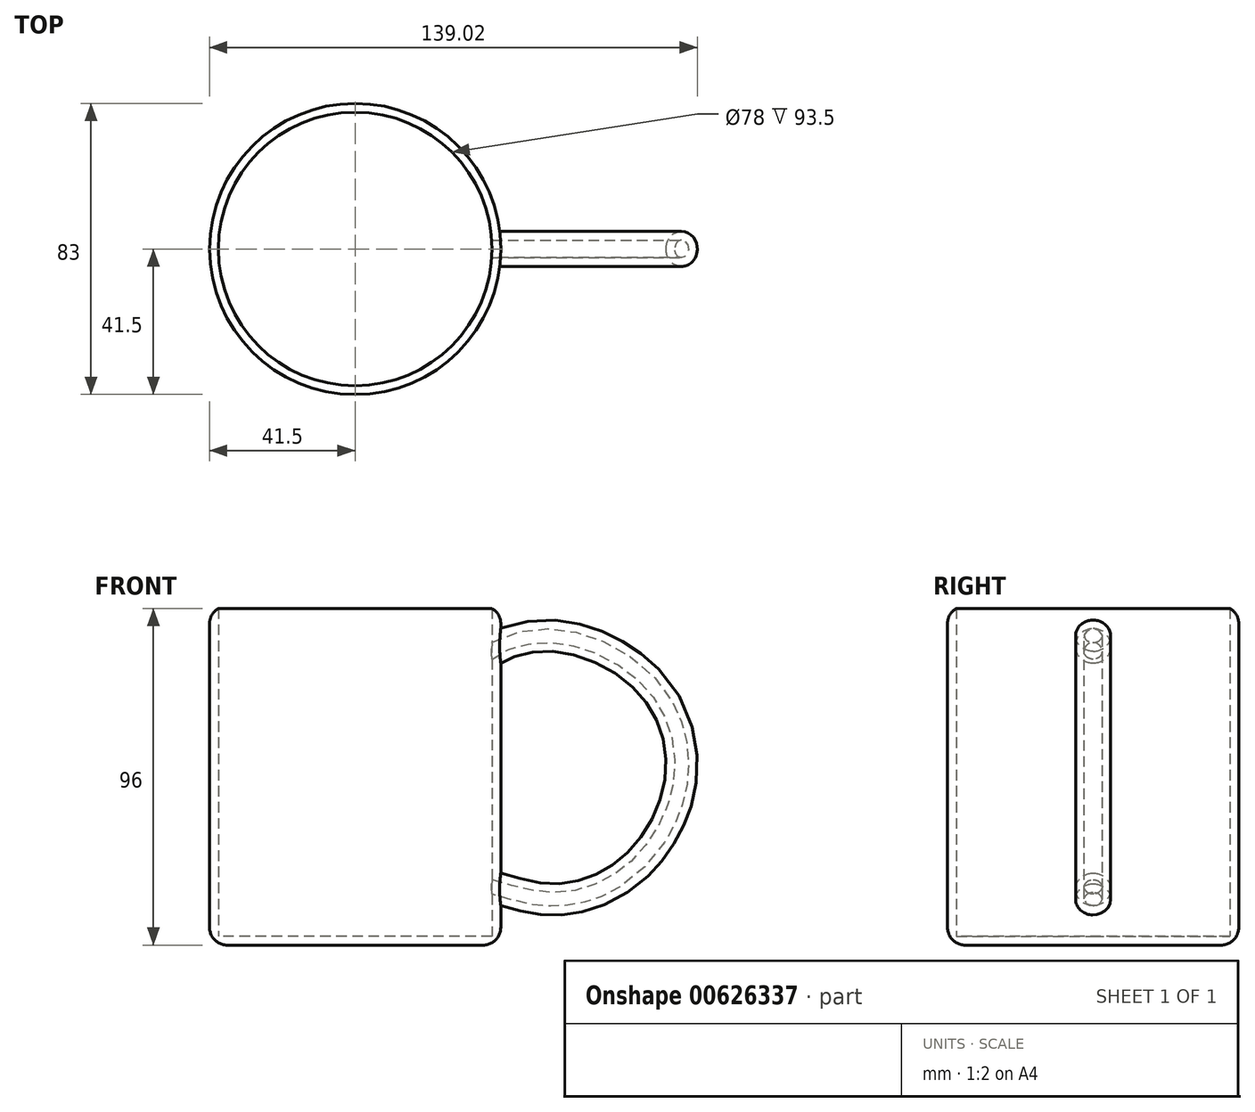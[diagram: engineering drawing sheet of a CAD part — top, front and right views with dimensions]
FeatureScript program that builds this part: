
annotation { "Feature Type Name" : "Feature", "Feature Type Description" : "" }
export const myFeature = defineFeature(function(context is Context, id is Id, definition is map)
    precondition{}
    {
        {
            var Q0;
            Q0=qCreatedBy(makeId("Top.planeOp"),FACE);
            var sketch = newSketch(context, id + "F0", { "sketchPlane" : qUnion([Q0])});
            skCircle(sketch, "E0", {"center": v(0, 0) * mm, "radius": 41.5 * mm});
            skSolve(sketch);
        }
        {
            var Q0;
            Q0 = qSketchRegion(id + "F0", true);
            extrude(context, id + "F1", {"entities" : qUnion([Q0]), "depth" : 96 * mm, "offsetDistance" : 25 * mm});
        }
        {
            var Q0;
            Q0=qCreatedBy(makeId("Front.planeOp"),FACE);
            var sketch = newSketch(context, id + "F2", { "sketchPlane" : qUnion([Q0])});
            skFitSpline(sketch, "E1", {"points": [v(38.23, 83.16) * mm, v(57.55, 88.06) * mm, v(85.9, 72.62) * mm, v(92.41, 44.95) * mm, v(77.3, 20.28) * mm, v(53.06, 13.24) * mm, v(32.68, 17.57) * mm], "startDerivative": vector(69.13, 66.04) * mm, "endDerivative": vector(-96.94, -2.26) * mm});
            skSolve(sketch);
        }
        {
            var Q0;
            Q0=qCreatedBy(makeId("Right.planeOp"),FACE);
            cPlane(context, id + "F3", {"entities" : qUnion([Q0]), "cplaneType" : CPlaneType.OFFSET, "offset" : 41.5 * mm, "width" : 150 * mm, "height" : 150 * mm});
        }
        {
            var Q0;
            Q0=qCreatedBy(id+"F3.planeOp",FACE);
            var sketch = newSketch(context, id + "F4", { "sketchPlane" : qUnion([Q0])});
            skCircle(sketch, "E2", {"center": v(0, 85.35) * mm, "radius": 5 * mm});
            skSolve(sketch);
        }
        {
            var Q0;
            Q0=makeQuery(id+"F4.imprint","IMPRINT",FACE,{"disambiguationData":[TD([[makeQuery(id+"F4.imprint","IMPRINT",EDGE,{"derivedFrom":sQuery(id+"F4.wireOp",EDGE,"E2")}),1.0]])]});
            var Q1;
            Q1=sQuery(id+"F2.wireOp",EDGE,"E1");
            sweep(context, id + "F5", {"operationType" : NewBodyOperationType.ADD, "profiles" : qUnion([Q0]), "path" : qUnion([Q1])});
        }
        {
            var Q0;
            Q0=makeQuery(id+"F1.opExtrude","CAP_FACE",FACE,{"disambiguationData":[OSD([sQuery(id+"F0.wireOp",EDGE,"E0")])],"isStart":false});
            shell(context, id + "F6", {"entities" : qUnion([Q0]), "thickness" : 2.5 * mm});
        }
        {
            var Q0;
            Q0=makeQuery(id+"F1.opExtrude","CAP_EDGE",EDGE,{"disambiguationData":[OSD([sQuery(id+"F0.wireOp",EDGE,"E0")])],"isStart":false});
            var Q1;
            Q1=makeQuery(id+"F1.opExtrude","CAP_EDGE",EDGE,{"disambiguationData":[OSD([sQuery(id+"F0.wireOp",EDGE,"E0")])],"isStart":true});
            fillet(context, id + "F7", {"entities" : qUnion([Q0, Q1]), "radius" : 5 * mm, "tangentPropagation" : true, "allowEdgeOverflow" : false});
        }
    });
